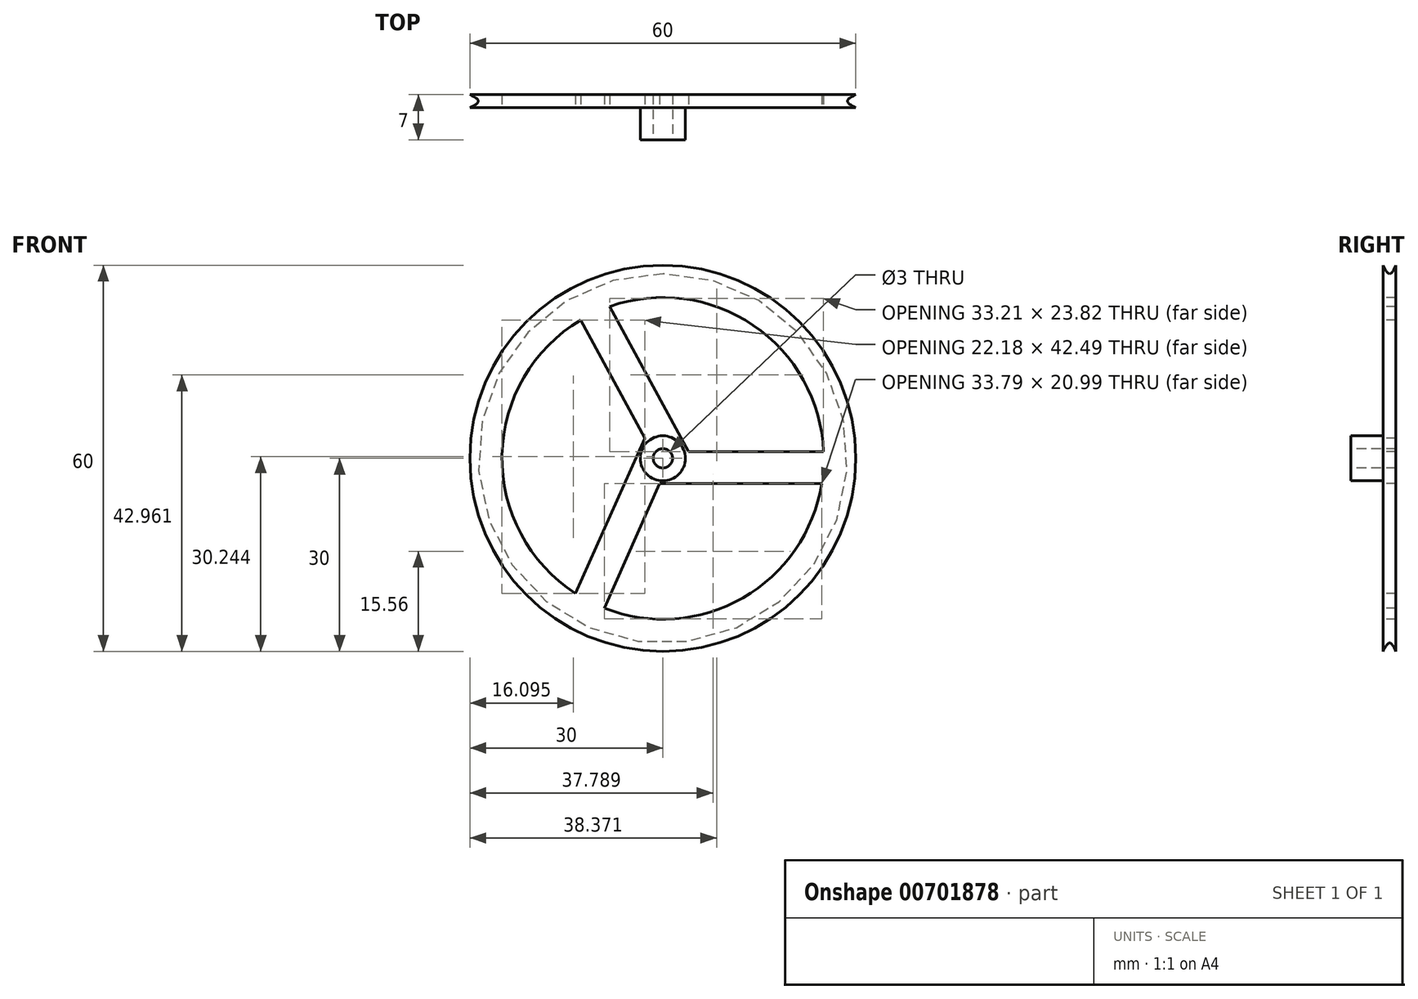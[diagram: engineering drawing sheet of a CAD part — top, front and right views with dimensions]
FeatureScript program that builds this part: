
annotation { "Feature Type Name" : "Feature", "Feature Type Description" : "" }
export const myFeature = defineFeature(function(context is Context, id is Id, definition is map)
    precondition{}
    {
        {
            var Q0;
            Q0=qCreatedBy(makeId("Top.planeOp"),FACE);
            var sketch = newSketch(context, id + "F0", { "sketchPlane" : qUnion([Q0])});
            skLineSegment(sketch, "E0", {"start": v(0, 0) * mm, "end": v(-30, 0) * mm});
            skLineSegment(sketch, "E1", {"start": v(-30, 2) * mm, "end": v(0, 2) * mm});
            skLineSegment(sketch, "E2", {"start": v(0, 2) * mm, "end": v(0, 0) * mm});
            skFitSpline(sketch, "E3", {"points": [v(-30, 2) * mm, v(-28.68, 1.01) * mm, v(-30, 0) * mm], "startDerivative": vector(6.98, -3.34) * mm, "endDerivative": vector(-6.56, -2.97) * mm});
            skSolve(sketch);
        }
        {
            var Q0;
            Q0=makeQuery(id+"F0.imprint","IMPRINT",FACE,{"disambiguationData":[TD([[makeQuery(id+"F0.imprint","IMPRINT",EDGE,{"derivedFrom":sQuery(id+"F0.wireOp",EDGE,"E0")}),-1.0]])]});
            var Q1;
            Q1=sQuery(id+"F0.wireOp",EDGE,"E2");
            revolve(context, id + "F1", {"entities" : qUnion([Q0]), "axis" : qUnion([Q1]), "revolveType" : RevolveType.FULL});
        }
        {
            var Q0;
            Q0=qCreatedBy(makeId("Front.planeOp"),FACE);
            var sketch = newSketch(context, id + "F2", { "sketchPlane" : qUnion([Q0])});
            skCircle(sketch, "E4", {"center": v(0, 0) * mm, "radius": 1.5 * mm});
            skCircle(sketch, "E5", {"center": v(0, 0) * mm, "radius": 3.5 * mm});
            skCircle(sketch, "E6", {"center": v(0, 0) * mm, "radius": 25 * mm});
            skSolve(sketch);
        }
        {
            var Q0;
            Q0=makeQuery(id+"F2.imprint","IMPRINT",FACE,{"disambiguationData":[TD([[makeQuery(id+"F2.imprint","IMPRINT",EDGE,{"derivedFrom":sQuery(id+"F2.wireOp",EDGE,"E4")}),1.0]])]});
            var Q1;
            Q1=makeQuery(id+"F2.imprint","IMPRINT",FACE,{"disambiguationData":[TD([[makeQuery(id+"F2.imprint","IMPRINT",EDGE,{"derivedFrom":sQuery(id+"F2.wireOp",EDGE,"E5")}),-1.0]])]});
            extrude(context, id + "F3", {"entities" : qUnion([Q0, Q1]), "operationType" : NewBodyOperationType.REMOVE, "oppositeDirection" : true, "depth" : 1000 * mm, "offsetDistance" : 25 * mm});
        }
        {
            var Q0;
            Q0=qCreatedBy(makeId("Front.planeOp"),FACE);
            var sketch = newSketch(context, id + "F4", { "sketchPlane" : qUnion([Q0])});
            skLineSegment(sketch, "E7", {"start": v(-14.07, -22.13) * mm, "end": v(-9.5, -24.16) * mm});
            skLineSegment(sketch, "E8", {"start": v(25.75, -3.95) * mm, "end": v(25.75, 1.05) * mm});
            skLineSegment(sketch, "E9", {"start": v(-13.19, 22.25) * mm, "end": v(-8.8, 24.63) * mm});
            skLineSegment(sketch, "E10", {"start": v(-9.5, -24.16) * mm, "end": v(-0.5, -3.95) * mm});
            skLineSegment(sketch, "E11", {"start": v(-0.5, -3.95) * mm, "end": v(25.75, -3.95) * mm});
            skLineSegment(sketch, "E12", {"start": v(-8.8, 24.63) * mm, "end": v(4, 1.05) * mm});
            skLineSegment(sketch, "E13", {"start": v(4, 1.05) * mm, "end": v(25.75, 1.05) * mm});
            skLineSegment(sketch, "E14", {"start": v(-13.19, 22.25) * mm, "end": v(-2.81, 3.13) * mm});
            skLineSegment(sketch, "E15", {"start": v(-14.07, -22.13) * mm, "end": v(-2.81, 3.13) * mm});
            skSolve(sketch);
        }
        {
            var Q0;
            Q0=makeQuery(id+"F4.imprint","IMPRINT",FACE,{"disambiguationData":[TD([[makeQuery(id+"F4.imprint","IMPRINT",EDGE,{"derivedFrom":sQuery(id+"F4.wireOp",EDGE,"E7")}),1.0]])]});
            extrude(context, id + "F5", {"entities" : qUnion([Q0]), "operationType" : NewBodyOperationType.ADD, "oppositeDirection" : true, "depth" : 2 * mm, "offsetDistance" : 25 * mm});
        }
        {
            var Q0;
            Q0=makeQuery(id+"F2.imprint","IMPRINT",FACE,{"disambiguationData":[TD([[makeQuery(id+"F2.imprint","IMPRINT",EDGE,{"derivedFrom":sQuery(id+"F2.wireOp",EDGE,"E4")}),1.0]])]});
            extrude(context, id + "F6", {"entities" : qUnion([Q0]), "operationType" : NewBodyOperationType.REMOVE, "endBound" : BoundingType.SYMMETRIC, "oppositeDirection" : true, "depth" : 1050 * mm, "offsetDistance" : 25 * mm});
        }
        {
            var Q0;
            Q0=makeQuery(id+"F2.imprint","IMPRINT",FACE,{"disambiguationData":[TD([[makeQuery(id+"F2.imprint","IMPRINT",EDGE,{"derivedFrom":sQuery(id+"F2.wireOp",EDGE,"E4")}),-1.0]])]});
            extrude(context, id + "F7", {"entities" : qUnion([Q0]), "operationType" : NewBodyOperationType.ADD, "depth" : 5 * mm, "offsetDistance" : 25 * mm});
        }
    });
